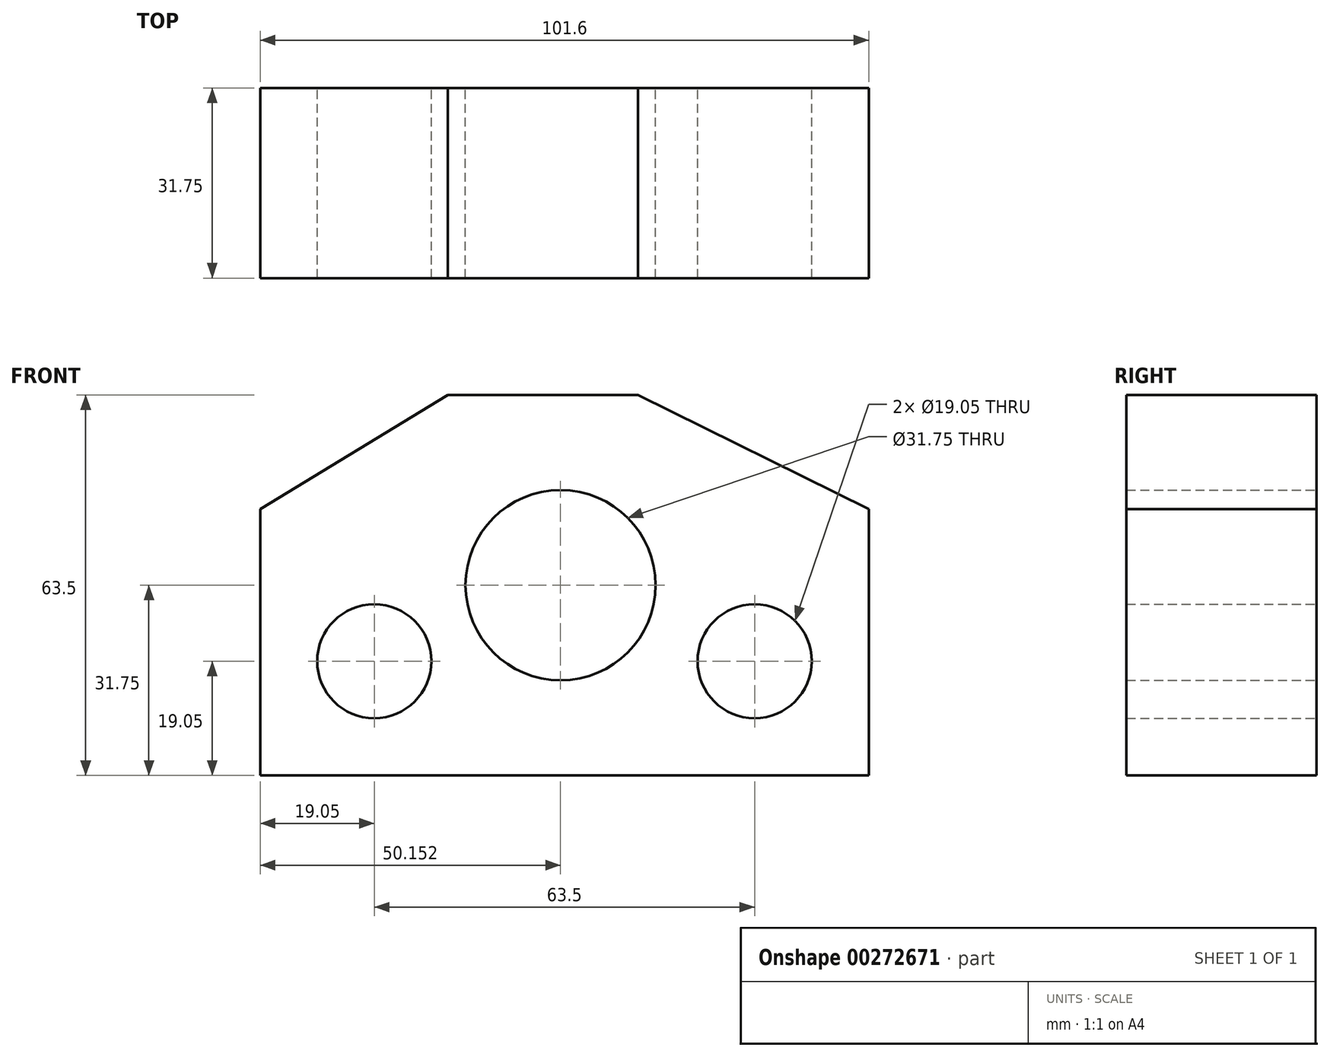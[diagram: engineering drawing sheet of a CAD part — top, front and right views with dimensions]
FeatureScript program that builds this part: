
annotation { "Feature Type Name" : "Feature", "Feature Type Description" : "" }
export const myFeature = defineFeature(function(context is Context, id is Id, definition is map)
    precondition{}
    {
        {
            var Q0;
            Q0=qCreatedBy(makeId("Front.planeOp"),FACE);
            var sketch = newSketch(context, id + "F0", { "sketchPlane" : qUnion([Q0])});
            skLineSegment(sketch, "E0", {"start": v(-63.05, 0) * mm, "end": v(-63.05, 44.45) * mm});
            skLineSegment(sketch, "E1", {"start": v(-63.05, 44.45) * mm, "end": v(-31.75, 63.5) * mm});
            skLineSegment(sketch, "E2", {"start": v(-31.75, 63.5) * mm, "end": v(0, 63.5) * mm});
            skLineSegment(sketch, "E3", {"start": v(0, 63.5) * mm, "end": v(38.55, 44.45) * mm});
            skLineSegment(sketch, "E4", {"start": v(38.55, 44.45) * mm, "end": v(38.55, 0) * mm});
            skLineSegment(sketch, "E5", {"start": v(38.55, 0) * mm, "end": v(-63.05, 0) * mm});
            skCircle(sketch, "E6", {"center": v(-12.9, 31.75) * mm, "radius": 15.88 * mm});
            skCircle(sketch, "E7", {"center": v(19.5, 19.05) * mm, "radius": 9.53 * mm});
            skCircle(sketch, "E8", {"center": v(-44, 19.05) * mm, "radius": 9.53 * mm});
            skSolve(sketch);
        }
        {
            var Q0;
            Q0=makeQuery(id+"F0.imprint","IMPRINT",FACE,{"disambiguationData":[TD([[makeQuery(id+"F0.imprint","IMPRINT",EDGE,{"derivedFrom":sQuery(id+"F0.wireOp",EDGE,"E0")}),-1.0]])]});
            extrude(context, id + "F1", {"entities" : qUnion([Q0]), "depth" : 31.75 * mm});
        }
    });
